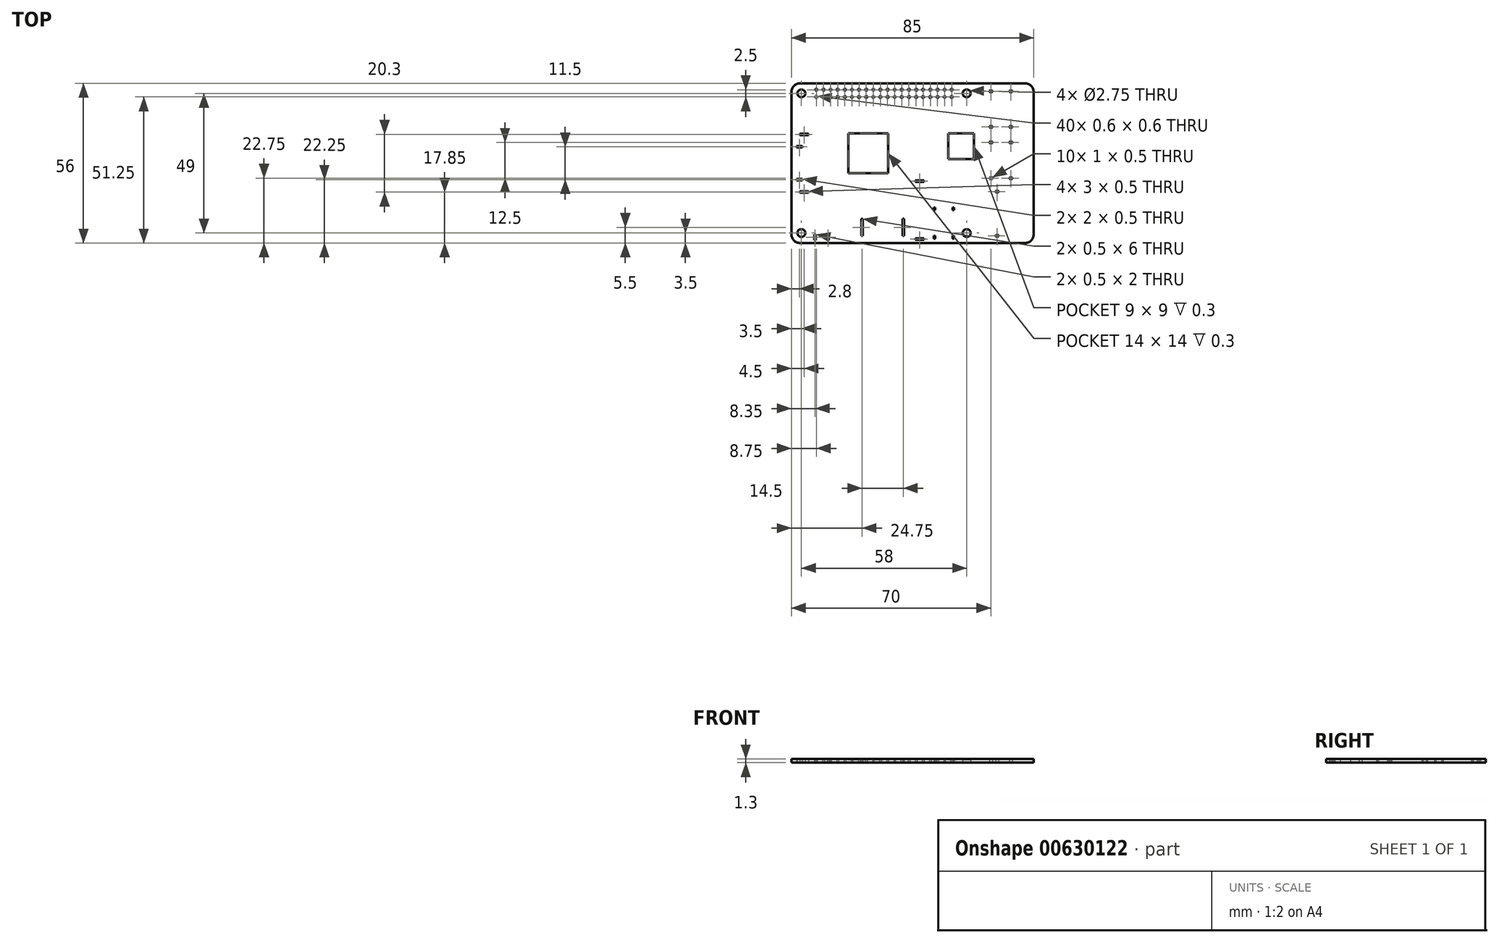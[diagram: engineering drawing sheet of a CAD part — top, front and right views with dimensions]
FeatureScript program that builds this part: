
annotation { "Feature Type Name" : "Feature", "Feature Type Description" : "" }
export const myFeature = defineFeature(function(context is Context, id is Id, definition is map)
    precondition{}
    {
        {
            var Q0;
            Q0=qCreatedBy(makeId("Top.planeOp"),FACE);
            var sketch = newSketch(context, id + "F0", { "sketchPlane" : qUnion([Q0])});
            skLineSegment(sketch, "E0.bottom", {"start": v(0, 0) * mm, "end": v(85, 0) * mm});
            skLineSegment(sketch, "E0.top", {"start": v(0, 56) * mm, "end": v(85, 56) * mm});
            skLineSegment(sketch, "E0.left", {"start": v(0, 0) * mm, "end": v(0, 56) * mm});
            skLineSegment(sketch, "E0.right", {"start": v(85, 0) * mm, "end": v(85, 56) * mm});
            skCircle(sketch, "E1", {"center": v(3.5, 52.5) * mm, "radius": 1.38 * mm});
            skCircle(sketch, "E2", {"center": v(61.5, 52.5) * mm, "radius": 1.38 * mm});
            skCircle(sketch, "E3", {"center": v(61.5, 3.5) * mm, "radius": 1.38 * mm});
            skCircle(sketch, "E4", {"center": v(3.5, 3.5) * mm, "radius": 1.37 * mm});
            skLineSegment(sketch, "E5.bottom", {"start": v(7.5, 55) * mm, "end": v(57.5, 55) * mm, "construction": true});
            skLineSegment(sketch, "E5.top", {"start": v(7.5, 50) * mm, "end": v(57.5, 50) * mm, "construction": true});
            skLineSegment(sketch, "E5.left", {"start": v(7.5, 55) * mm, "end": v(7.5, 50) * mm, "construction": true});
            skLineSegment(sketch, "E5.right", {"start": v(57.5, 55) * mm, "end": v(57.5, 50) * mm, "construction": true});
            skLineSegment(sketch, "E6", {"start": v(32.5, 55) * mm, "end": v(32.5, 50) * mm, "construction": true});
            skLineSegment(sketch, "E7", {"start": v(7.5, 52.5) * mm, "end": v(57.5, 52.5) * mm, "construction": true});
            skLineSegment(sketch, "E8.bottom", {"start": v(8.45, 54.05) * mm, "end": v(9.05, 54.05) * mm});
            skLineSegment(sketch, "E8.top", {"start": v(8.45, 53.45) * mm, "end": v(9.05, 53.45) * mm});
            skLineSegment(sketch, "E8.left", {"start": v(8.45, 54.05) * mm, "end": v(8.45, 53.45) * mm});
            skLineSegment(sketch, "E8.right", {"start": v(9.05, 54.05) * mm, "end": v(9.05, 53.45) * mm});
            skLineSegment(sketch, "E9", {"start": v(10, 55) * mm, "end": v(10, 50) * mm, "construction": true});
            skLineSegment(sketch, "E10.1.0.0", {"start": v(10.95, 53.45) * mm, "end": v(11.55, 53.45) * mm});
            skLineSegment(sketch, "E10.1.0.1", {"start": v(10.95, 54.05) * mm, "end": v(11.55, 54.05) * mm});
            skLineSegment(sketch, "E10.1.0.2", {"start": v(11.55, 54.05) * mm, "end": v(11.55, 53.45) * mm});
            skLineSegment(sketch, "E10.1.0.3", {"start": v(10.95, 54.05) * mm, "end": v(10.95, 53.45) * mm});
            skLineSegment(sketch, "E10.2.0.0", {"start": v(13.45, 53.45) * mm, "end": v(14.05, 53.45) * mm});
            skLineSegment(sketch, "E10.2.0.1", {"start": v(13.45, 54.05) * mm, "end": v(14.05, 54.05) * mm});
            skLineSegment(sketch, "E10.2.0.2", {"start": v(14.05, 54.05) * mm, "end": v(14.05, 53.45) * mm});
            skLineSegment(sketch, "E10.2.0.3", {"start": v(13.45, 54.05) * mm, "end": v(13.45, 53.45) * mm});
            skLineSegment(sketch, "E10.3.0.0", {"start": v(15.95, 53.45) * mm, "end": v(16.55, 53.45) * mm});
            skLineSegment(sketch, "E10.3.0.1", {"start": v(15.95, 54.05) * mm, "end": v(16.55, 54.05) * mm});
            skLineSegment(sketch, "E10.3.0.2", {"start": v(16.55, 54.05) * mm, "end": v(16.55, 53.45) * mm});
            skLineSegment(sketch, "E10.3.0.3", {"start": v(15.95, 54.05) * mm, "end": v(15.95, 53.45) * mm});
            skLineSegment(sketch, "E10.4.0.0", {"start": v(18.45, 53.45) * mm, "end": v(19.05, 53.45) * mm});
            skLineSegment(sketch, "E10.4.0.1", {"start": v(18.45, 54.05) * mm, "end": v(19.05, 54.05) * mm});
            skLineSegment(sketch, "E10.4.0.2", {"start": v(19.05, 54.05) * mm, "end": v(19.05, 53.45) * mm});
            skLineSegment(sketch, "E10.4.0.3", {"start": v(18.45, 54.05) * mm, "end": v(18.45, 53.45) * mm});
            skLineSegment(sketch, "E10.5.0.0", {"start": v(20.95, 53.45) * mm, "end": v(21.55, 53.45) * mm});
            skLineSegment(sketch, "E10.5.0.1", {"start": v(20.95, 54.05) * mm, "end": v(21.55, 54.05) * mm});
            skLineSegment(sketch, "E10.5.0.2", {"start": v(21.55, 54.05) * mm, "end": v(21.55, 53.45) * mm});
            skLineSegment(sketch, "E10.5.0.3", {"start": v(20.95, 54.05) * mm, "end": v(20.95, 53.45) * mm});
            skLineSegment(sketch, "E10.6.0.0", {"start": v(23.45, 53.45) * mm, "end": v(24.05, 53.45) * mm});
            skLineSegment(sketch, "E10.6.0.1", {"start": v(23.45, 54.05) * mm, "end": v(24.05, 54.05) * mm});
            skLineSegment(sketch, "E10.6.0.2", {"start": v(24.05, 54.05) * mm, "end": v(24.05, 53.45) * mm});
            skLineSegment(sketch, "E10.6.0.3", {"start": v(23.45, 54.05) * mm, "end": v(23.45, 53.45) * mm});
            skLineSegment(sketch, "E10.7.0.0", {"start": v(25.95, 53.45) * mm, "end": v(26.55, 53.45) * mm});
            skLineSegment(sketch, "E10.7.0.1", {"start": v(25.95, 54.05) * mm, "end": v(26.55, 54.05) * mm});
            skLineSegment(sketch, "E10.7.0.2", {"start": v(26.55, 54.05) * mm, "end": v(26.55, 53.45) * mm});
            skLineSegment(sketch, "E10.7.0.3", {"start": v(25.95, 54.05) * mm, "end": v(25.95, 53.45) * mm});
            skLineSegment(sketch, "E10.8.0.0", {"start": v(28.45, 53.45) * mm, "end": v(29.05, 53.45) * mm});
            skLineSegment(sketch, "E10.8.0.1", {"start": v(28.45, 54.05) * mm, "end": v(29.05, 54.05) * mm});
            skLineSegment(sketch, "E10.8.0.2", {"start": v(29.05, 54.05) * mm, "end": v(29.05, 53.45) * mm});
            skLineSegment(sketch, "E10.8.0.3", {"start": v(28.45, 54.05) * mm, "end": v(28.45, 53.45) * mm});
            skLineSegment(sketch, "E10.9.0.0", {"start": v(30.95, 53.45) * mm, "end": v(31.55, 53.45) * mm});
            skLineSegment(sketch, "E10.9.0.1", {"start": v(30.95, 54.05) * mm, "end": v(31.55, 54.05) * mm});
            skLineSegment(sketch, "E10.9.0.2", {"start": v(31.55, 54.05) * mm, "end": v(31.55, 53.45) * mm});
            skLineSegment(sketch, "E10.9.0.3", {"start": v(30.95, 54.05) * mm, "end": v(30.95, 53.45) * mm});
            skLineSegment(sketch, "E10.direction1", {"start": v(8.45, 53.45) * mm, "end": v(10.95, 53.45) * mm, "construction": true});
            skLineSegment(sketch, "E11.MirrorCS", {"start": v(28.45, 51.55) * mm, "end": v(29.05, 51.55) * mm});
            skLineSegment(sketch, "E12.MirrorCS", {"start": v(28.45, 50.95) * mm, "end": v(29.05, 50.95) * mm});
            skLineSegment(sketch, "E13.MirrorCS", {"start": v(30.95, 50.95) * mm, "end": v(31.55, 50.95) * mm});
            skLineSegment(sketch, "E14.MirrorCS", {"start": v(10.95, 50.95) * mm, "end": v(11.55, 50.95) * mm});
            skLineSegment(sketch, "E15.MirrorCS", {"start": v(10.95, 51.55) * mm, "end": v(11.55, 51.55) * mm});
            skLineSegment(sketch, "E16.MirrorCS", {"start": v(30.95, 51.55) * mm, "end": v(31.55, 51.55) * mm});
            skLineSegment(sketch, "E17.MirrorCS", {"start": v(8.45, 50.95) * mm, "end": v(9.05, 50.95) * mm});
            skLineSegment(sketch, "E18.MirrorCS", {"start": v(8.45, 51.55) * mm, "end": v(9.05, 51.55) * mm});
            skLineSegment(sketch, "E19.MirrorCS", {"start": v(9.05, 50.95) * mm, "end": v(9.05, 51.55) * mm});
            skLineSegment(sketch, "E20.MirrorCS", {"start": v(18.45, 50.95) * mm, "end": v(18.45, 51.55) * mm});
            skLineSegment(sketch, "E21.MirrorCS", {"start": v(28.45, 50.95) * mm, "end": v(28.45, 51.55) * mm});
            skLineSegment(sketch, "E22.MirrorCS", {"start": v(20.95, 50.95) * mm, "end": v(20.95, 51.55) * mm});
            skLineSegment(sketch, "E23.MirrorCS", {"start": v(18.45, 51.55) * mm, "end": v(19.05, 51.55) * mm});
            skLineSegment(sketch, "E24.MirrorCS", {"start": v(30.95, 50.95) * mm, "end": v(30.95, 51.55) * mm});
            skLineSegment(sketch, "E25.MirrorCS", {"start": v(10.95, 50.95) * mm, "end": v(10.95, 51.55) * mm});
            skLineSegment(sketch, "E26.MirrorCS", {"start": v(14.05, 50.95) * mm, "end": v(14.05, 51.55) * mm});
            skLineSegment(sketch, "E27.MirrorCS", {"start": v(24.05, 50.95) * mm, "end": v(24.05, 51.55) * mm});
            skLineSegment(sketch, "E28.MirrorCS", {"start": v(19.05, 50.95) * mm, "end": v(19.05, 51.55) * mm});
            skLineSegment(sketch, "E29.MirrorCS", {"start": v(29.05, 50.95) * mm, "end": v(29.05, 51.55) * mm});
            skLineSegment(sketch, "E30.MirrorCS", {"start": v(21.55, 50.95) * mm, "end": v(21.55, 51.55) * mm});
            skLineSegment(sketch, "E31.MirrorCS", {"start": v(15.95, 50.95) * mm, "end": v(15.95, 51.55) * mm});
            skLineSegment(sketch, "E32.MirrorCS", {"start": v(31.55, 50.95) * mm, "end": v(31.55, 51.55) * mm});
            skLineSegment(sketch, "E33.MirrorCS", {"start": v(25.95, 50.95) * mm, "end": v(25.95, 51.55) * mm});
            skLineSegment(sketch, "E34.MirrorCS", {"start": v(11.55, 50.95) * mm, "end": v(11.55, 51.55) * mm});
            skLineSegment(sketch, "E35.MirrorCS", {"start": v(13.45, 50.95) * mm, "end": v(14.05, 50.95) * mm});
            skLineSegment(sketch, "E36.MirrorCS", {"start": v(23.45, 50.95) * mm, "end": v(24.05, 50.95) * mm});
            skLineSegment(sketch, "E37.MirrorCS", {"start": v(15.95, 50.95) * mm, "end": v(16.55, 50.95) * mm});
            skLineSegment(sketch, "E38.MirrorCS", {"start": v(25.95, 50.95) * mm, "end": v(26.55, 50.95) * mm});
            skLineSegment(sketch, "E39.MirrorCS", {"start": v(18.45, 50.95) * mm, "end": v(19.05, 50.95) * mm});
            skLineSegment(sketch, "E40.MirrorCS", {"start": v(8.45, 50.95) * mm, "end": v(8.45, 51.55) * mm});
            skLineSegment(sketch, "E41.MirrorCS", {"start": v(20.95, 50.95) * mm, "end": v(21.55, 50.95) * mm});
            skLineSegment(sketch, "E42.MirrorCS", {"start": v(16.55, 50.95) * mm, "end": v(16.55, 51.55) * mm});
            skLineSegment(sketch, "E43.MirrorCS", {"start": v(26.55, 50.95) * mm, "end": v(26.55, 51.55) * mm});
            skLineSegment(sketch, "E44.MirrorCS", {"start": v(13.45, 51.55) * mm, "end": v(14.05, 51.55) * mm});
            skLineSegment(sketch, "E45.MirrorCS", {"start": v(23.45, 51.55) * mm, "end": v(24.05, 51.55) * mm});
            skLineSegment(sketch, "E46.MirrorCS", {"start": v(8.45, 51.55) * mm, "end": v(10.95, 51.55) * mm, "construction": true});
            skLineSegment(sketch, "E47.MirrorCS", {"start": v(15.95, 51.55) * mm, "end": v(16.55, 51.55) * mm});
            skLineSegment(sketch, "E48.MirrorCS", {"start": v(25.95, 51.55) * mm, "end": v(26.55, 51.55) * mm});
            skLineSegment(sketch, "E49.MirrorCS", {"start": v(13.45, 50.95) * mm, "end": v(13.45, 51.55) * mm});
            skLineSegment(sketch, "E50.MirrorCS", {"start": v(23.45, 50.95) * mm, "end": v(23.45, 51.55) * mm});
            skLineSegment(sketch, "E51.MirrorCS", {"start": v(20.95, 51.55) * mm, "end": v(21.55, 51.55) * mm});
            skLineSegment(sketch, "E52.MirrorCS", {"start": v(49.05, 50.95) * mm, "end": v(48.45, 50.95) * mm});
            skLineSegment(sketch, "E53.MirrorCS", {"start": v(41.55, 50.95) * mm, "end": v(40.95, 50.95) * mm});
            skLineSegment(sketch, "E54.MirrorCS", {"start": v(41.55, 54.05) * mm, "end": v(40.95, 54.05) * mm});
            skLineSegment(sketch, "E55.MirrorCS", {"start": v(46.55, 54.05) * mm, "end": v(45.95, 54.05) * mm});
            skLineSegment(sketch, "E56.MirrorCS", {"start": v(41.55, 53.45) * mm, "end": v(40.95, 53.45) * mm});
            skLineSegment(sketch, "E57.MirrorCS", {"start": v(44.05, 51.55) * mm, "end": v(43.45, 51.55) * mm});
            skLineSegment(sketch, "E58.MirrorCS", {"start": v(41.55, 51.55) * mm, "end": v(40.95, 51.55) * mm});
            skLineSegment(sketch, "E59.MirrorCS", {"start": v(49.05, 54.05) * mm, "end": v(48.45, 54.05) * mm});
            skLineSegment(sketch, "E60.MirrorCS", {"start": v(49.05, 51.55) * mm, "end": v(48.45, 51.55) * mm});
            skLineSegment(sketch, "E61.MirrorCS", {"start": v(44.05, 53.45) * mm, "end": v(43.45, 53.45) * mm});
            skLineSegment(sketch, "E62.MirrorCS", {"start": v(49.05, 53.45) * mm, "end": v(48.45, 53.45) * mm});
            skLineSegment(sketch, "E63.MirrorCS", {"start": v(46.55, 50.95) * mm, "end": v(45.95, 50.95) * mm});
            skLineSegment(sketch, "E64.MirrorCS", {"start": v(46.55, 51.55) * mm, "end": v(45.95, 51.55) * mm});
            skLineSegment(sketch, "E65.MirrorCS", {"start": v(44.05, 54.05) * mm, "end": v(43.45, 54.05) * mm});
            skLineSegment(sketch, "E66.MirrorCS", {"start": v(44.05, 50.95) * mm, "end": v(43.45, 50.95) * mm});
            skLineSegment(sketch, "E67.MirrorCS", {"start": v(46.55, 53.45) * mm, "end": v(45.95, 53.45) * mm});
            skLineSegment(sketch, "E68.MirrorCS", {"start": v(55.95, 54.05) * mm, "end": v(55.95, 53.45) * mm});
            skLineSegment(sketch, "E69.MirrorCS", {"start": v(56.55, 53.45) * mm, "end": v(55.95, 53.45) * mm});
            skLineSegment(sketch, "E70.MirrorCS", {"start": v(56.55, 51.55) * mm, "end": v(55.95, 51.55) * mm});
            skLineSegment(sketch, "E71.MirrorCS", {"start": v(46.55, 54.05) * mm, "end": v(46.55, 53.45) * mm});
            skLineSegment(sketch, "E72.MirrorCS", {"start": v(36.55, 54.05) * mm, "end": v(36.55, 53.45) * mm});
            skLineSegment(sketch, "E73.MirrorCS", {"start": v(36.55, 50.95) * mm, "end": v(36.55, 51.55) * mm});
            skLineSegment(sketch, "E74.MirrorCS", {"start": v(45.95, 50.95) * mm, "end": v(45.95, 51.55) * mm});
            skLineSegment(sketch, "E75.MirrorCS", {"start": v(51.55, 51.55) * mm, "end": v(50.95, 51.55) * mm});
            skLineSegment(sketch, "E76.MirrorCS", {"start": v(50.95, 54.05) * mm, "end": v(50.95, 53.45) * mm});
            skLineSegment(sketch, "E77.MirrorCS", {"start": v(40.95, 54.05) * mm, "end": v(40.95, 53.45) * mm});
            skLineSegment(sketch, "E78.MirrorCS", {"start": v(36.55, 50.95) * mm, "end": v(35.95, 50.95) * mm});
            skLineSegment(sketch, "E79.MirrorCS", {"start": v(45.95, 54.05) * mm, "end": v(45.95, 53.45) * mm});
            skLineSegment(sketch, "E80.MirrorCS", {"start": v(35.95, 54.05) * mm, "end": v(35.95, 53.45) * mm});
            skLineSegment(sketch, "E81.MirrorCS", {"start": v(46.55, 50.95) * mm, "end": v(46.55, 51.55) * mm});
            skLineSegment(sketch, "E82.MirrorCS", {"start": v(40.95, 50.95) * mm, "end": v(40.95, 51.55) * mm});
            skLineSegment(sketch, "E83.MirrorCS", {"start": v(38.45, 50.95) * mm, "end": v(38.45, 51.55) * mm});
            skLineSegment(sketch, "E84.MirrorCS", {"start": v(51.55, 54.05) * mm, "end": v(50.95, 54.05) * mm});
            skLineSegment(sketch, "E85.MirrorCS", {"start": v(36.55, 51.55) * mm, "end": v(35.95, 51.55) * mm});
            skLineSegment(sketch, "E86.MirrorCS", {"start": v(36.55, 54.05) * mm, "end": v(35.95, 54.05) * mm});
            skLineSegment(sketch, "E87.MirrorCS", {"start": v(55.95, 50.95) * mm, "end": v(55.95, 51.55) * mm});
            skLineSegment(sketch, "E88.MirrorCS", {"start": v(51.55, 50.95) * mm, "end": v(50.95, 50.95) * mm});
            skLineSegment(sketch, "E89.MirrorCS", {"start": v(56.55, 54.05) * mm, "end": v(56.55, 53.45) * mm});
            skLineSegment(sketch, "E90.MirrorCS", {"start": v(50.95, 50.95) * mm, "end": v(50.95, 51.55) * mm});
            skLineSegment(sketch, "E91.MirrorCS", {"start": v(48.45, 50.95) * mm, "end": v(48.45, 51.55) * mm});
            skLineSegment(sketch, "E92.MirrorCS", {"start": v(51.55, 53.45) * mm, "end": v(50.95, 53.45) * mm});
            skLineSegment(sketch, "E93.MirrorCS", {"start": v(56.55, 53.45) * mm, "end": v(54.05, 53.45) * mm, "construction": true});
            skLineSegment(sketch, "E94.MirrorCS", {"start": v(34.05, 50.95) * mm, "end": v(33.45, 50.95) * mm});
            skLineSegment(sketch, "E95.MirrorCS", {"start": v(41.55, 54.05) * mm, "end": v(41.55, 53.45) * mm});
            skLineSegment(sketch, "E96.MirrorCS", {"start": v(51.55, 54.05) * mm, "end": v(51.55, 53.45) * mm});
            skLineSegment(sketch, "E97.MirrorCS", {"start": v(35.95, 50.95) * mm, "end": v(35.95, 51.55) * mm});
            skLineSegment(sketch, "E98.MirrorCS", {"start": v(39.05, 54.05) * mm, "end": v(38.45, 54.05) * mm});
            skLineSegment(sketch, "E99.MirrorCS", {"start": v(54.05, 51.55) * mm, "end": v(53.45, 51.55) * mm});
            skLineSegment(sketch, "E100.MirrorCS", {"start": v(49.05, 50.95) * mm, "end": v(49.05, 51.55) * mm});
            skLineSegment(sketch, "E101.MirrorCS", {"start": v(53.45, 54.05) * mm, "end": v(53.45, 53.45) * mm});
            skLineSegment(sketch, "E102.MirrorCS", {"start": v(54.05, 53.45) * mm, "end": v(53.45, 53.45) * mm});
            skLineSegment(sketch, "E103.MirrorCS", {"start": v(39.05, 50.95) * mm, "end": v(38.45, 50.95) * mm});
            skLineSegment(sketch, "E104.MirrorCS", {"start": v(44.05, 50.95) * mm, "end": v(44.05, 51.55) * mm});
            skLineSegment(sketch, "E105.MirrorCS", {"start": v(34.05, 53.45) * mm, "end": v(33.45, 53.45) * mm});
            skLineSegment(sketch, "E106.MirrorCS", {"start": v(39.05, 50.95) * mm, "end": v(39.05, 51.55) * mm});
            skLineSegment(sketch, "E107.MirrorCS", {"start": v(56.55, 50.95) * mm, "end": v(56.55, 51.55) * mm});
            skLineSegment(sketch, "E108.MirrorCS", {"start": v(33.45, 54.05) * mm, "end": v(33.45, 53.45) * mm});
            skLineSegment(sketch, "E109.MirrorCS", {"start": v(56.55, 50.95) * mm, "end": v(55.95, 50.95) * mm});
            skLineSegment(sketch, "E110.MirrorCS", {"start": v(34.05, 50.95) * mm, "end": v(34.05, 51.55) * mm});
            skLineSegment(sketch, "E111.MirrorCS", {"start": v(39.05, 54.05) * mm, "end": v(39.05, 53.45) * mm});
            skLineSegment(sketch, "E112.MirrorCS", {"start": v(49.05, 54.05) * mm, "end": v(49.05, 53.45) * mm});
            skLineSegment(sketch, "E113.MirrorCS", {"start": v(43.45, 54.05) * mm, "end": v(43.45, 53.45) * mm});
            skLineSegment(sketch, "E114.MirrorCS", {"start": v(51.55, 50.95) * mm, "end": v(51.55, 51.55) * mm});
            skLineSegment(sketch, "E115.MirrorCS", {"start": v(54.05, 50.95) * mm, "end": v(53.45, 50.95) * mm});
            skLineSegment(sketch, "E116.MirrorCS", {"start": v(39.05, 53.45) * mm, "end": v(38.45, 53.45) * mm});
            skLineSegment(sketch, "E117.MirrorCS", {"start": v(56.55, 51.55) * mm, "end": v(54.05, 51.55) * mm, "construction": true});
            skLineSegment(sketch, "E118.MirrorCS", {"start": v(43.45, 50.95) * mm, "end": v(43.45, 51.55) * mm});
            skLineSegment(sketch, "E119.MirrorCS", {"start": v(54.05, 54.05) * mm, "end": v(53.45, 54.05) * mm});
            skLineSegment(sketch, "E120.MirrorCS", {"start": v(33.45, 50.95) * mm, "end": v(33.45, 51.55) * mm});
            skLineSegment(sketch, "E121.MirrorCS", {"start": v(34.05, 51.55) * mm, "end": v(33.45, 51.55) * mm});
            skLineSegment(sketch, "E122.MirrorCS", {"start": v(38.45, 54.05) * mm, "end": v(38.45, 53.45) * mm});
            skLineSegment(sketch, "E123.MirrorCS", {"start": v(34.05, 54.05) * mm, "end": v(33.45, 54.05) * mm});
            skLineSegment(sketch, "E124.MirrorCS", {"start": v(39.05, 51.55) * mm, "end": v(38.45, 51.55) * mm});
            skLineSegment(sketch, "E125.MirrorCS", {"start": v(56.55, 54.05) * mm, "end": v(55.95, 54.05) * mm});
            skLineSegment(sketch, "E126.MirrorCS", {"start": v(54.05, 54.05) * mm, "end": v(54.05, 53.45) * mm});
            skLineSegment(sketch, "E127.MirrorCS", {"start": v(53.45, 50.95) * mm, "end": v(53.45, 51.55) * mm});
            skLineSegment(sketch, "E128.MirrorCS", {"start": v(48.45, 54.05) * mm, "end": v(48.45, 53.45) * mm});
            skLineSegment(sketch, "E129.MirrorCS", {"start": v(54.05, 50.95) * mm, "end": v(54.05, 51.55) * mm});
            skLineSegment(sketch, "E130.MirrorCS", {"start": v(34.05, 54.05) * mm, "end": v(34.05, 53.45) * mm});
            skLineSegment(sketch, "E131.MirrorCS", {"start": v(36.55, 53.45) * mm, "end": v(35.95, 53.45) * mm});
            skLineSegment(sketch, "E132.MirrorCS", {"start": v(41.55, 50.95) * mm, "end": v(41.55, 51.55) * mm});
            skLineSegment(sketch, "E133.MirrorCS", {"start": v(44.05, 54.05) * mm, "end": v(44.05, 53.45) * mm});
            skLineSegment(sketch, "E134", {"start": v(0, 28) * mm, "end": v(85, 28) * mm, "construction": true});
            skLineSegment(sketch, "E135.bottom", {"start": v(1.8, 34) * mm, "end": v(3.8, 34) * mm});
            skLineSegment(sketch, "E135.top", {"start": v(1.8, 33.5) * mm, "end": v(3.8, 33.5) * mm});
            skLineSegment(sketch, "E135.left", {"start": v(1.8, 34) * mm, "end": v(1.8, 33.5) * mm});
            skLineSegment(sketch, "E135.right", {"start": v(3.8, 34) * mm, "end": v(3.8, 33.5) * mm});
            skLineSegment(sketch, "E136.MirrorCS", {"start": v(1.8, 22) * mm, "end": v(3.8, 22) * mm});
            skLineSegment(sketch, "E137.MirrorCS", {"start": v(3.8, 22) * mm, "end": v(3.8, 22.5) * mm});
            skLineSegment(sketch, "E138.MirrorCS", {"start": v(1.8, 22.5) * mm, "end": v(3.8, 22.5) * mm});
            skLineSegment(sketch, "E139.MirrorCS", {"start": v(1.8, 22) * mm, "end": v(1.8, 22.5) * mm});
            skLineSegment(sketch, "E140.bottom", {"start": v(24.5, 8.5) * mm, "end": v(25, 8.5) * mm});
            skLineSegment(sketch, "E140.top", {"start": v(24.5, 2.5) * mm, "end": v(25, 2.5) * mm});
            skLineSegment(sketch, "E140.left", {"start": v(24.5, 8.5) * mm, "end": v(24.5, 2.5) * mm});
            skLineSegment(sketch, "E140.right", {"start": v(25, 8.5) * mm, "end": v(25, 2.5) * mm});
            skLineSegment(sketch, "E141", {"start": v(32, 0) * mm, "end": v(32, 56) * mm, "construction": true});
            skLineSegment(sketch, "E142.MirrorCS", {"start": v(39.5, 2.5) * mm, "end": v(39, 2.5) * mm});
            skLineSegment(sketch, "E143.MirrorCS", {"start": v(39.5, 8.5) * mm, "end": v(39, 8.5) * mm});
            skLineSegment(sketch, "E144.MirrorCS", {"start": v(39.5, 8.5) * mm, "end": v(39.5, 2.5) * mm});
            skLineSegment(sketch, "E145.MirrorCS", {"start": v(39, 8.5) * mm, "end": v(39, 2.5) * mm});
            skLineSegment(sketch, "E146.bottom", {"start": v(8.1, 3) * mm, "end": v(8.6, 3) * mm});
            skLineSegment(sketch, "E146.top", {"start": v(8.1, 1) * mm, "end": v(8.6, 1) * mm});
            skLineSegment(sketch, "E146.left", {"start": v(8.1, 3) * mm, "end": v(8.1, 1) * mm});
            skLineSegment(sketch, "E146.right", {"start": v(8.6, 3) * mm, "end": v(8.6, 1) * mm});
            skLineSegment(sketch, "E147", {"start": v(10.6, 56) * mm, "end": v(10.6, 0) * mm, "construction": true});
            skLineSegment(sketch, "E148.MirrorCS", {"start": v(13.1, 1) * mm, "end": v(12.6, 1) * mm});
            skLineSegment(sketch, "E149.MirrorCS", {"start": v(13.1, 3) * mm, "end": v(12.6, 3) * mm});
            skLineSegment(sketch, "E150.MirrorCS", {"start": v(13.1, 3) * mm, "end": v(13.1, 1) * mm});
            skLineSegment(sketch, "E151.MirrorCS", {"start": v(12.6, 3) * mm, "end": v(12.6, 1) * mm});
            skLineSegment(sketch, "E152", {"start": v(53.5, 0) * mm, "end": v(53.5, 56) * mm, "construction": true});
            skLineSegment(sketch, "E153.bottom", {"start": v(50, 12.5) * mm, "end": v(50.5, 12.5) * mm});
            skLineSegment(sketch, "E153.top", {"start": v(50, 11.5) * mm, "end": v(50.5, 11.5) * mm});
            skLineSegment(sketch, "E153.left", {"start": v(50, 12.5) * mm, "end": v(50, 11.5) * mm});
            skLineSegment(sketch, "E153.right", {"start": v(50.5, 12.5) * mm, "end": v(50.5, 11.5) * mm});
            skLineSegment(sketch, "E154.bottom", {"start": v(50, 2.5) * mm, "end": v(50.5, 2.5) * mm});
            skLineSegment(sketch, "E154.top", {"start": v(50, 1.5) * mm, "end": v(50.5, 1.5) * mm});
            skLineSegment(sketch, "E154.left", {"start": v(50, 2.5) * mm, "end": v(50, 1.5) * mm});
            skLineSegment(sketch, "E154.right", {"start": v(50.5, 2.5) * mm, "end": v(50.5, 1.5) * mm});
            skLineSegment(sketch, "E155.MirrorCS", {"start": v(57, 11.5) * mm, "end": v(56.5, 11.5) * mm});
            skLineSegment(sketch, "E156.MirrorCS", {"start": v(57, 12.5) * mm, "end": v(56.5, 12.5) * mm});
            skLineSegment(sketch, "E157.MirrorCS", {"start": v(57, 1.5) * mm, "end": v(56.5, 1.5) * mm});
            skLineSegment(sketch, "E158.MirrorCS", {"start": v(57, 2.5) * mm, "end": v(56.5, 2.5) * mm});
            skLineSegment(sketch, "E159.MirrorCS", {"start": v(56.5, 2.5) * mm, "end": v(56.5, 1.5) * mm});
            skLineSegment(sketch, "E160.MirrorCS", {"start": v(57, 2.5) * mm, "end": v(57, 1.5) * mm});
            skLineSegment(sketch, "E161.MirrorCS", {"start": v(57, 12.5) * mm, "end": v(57, 11.5) * mm});
            skLineSegment(sketch, "E162.MirrorCS", {"start": v(56.5, 12.5) * mm, "end": v(56.5, 11.5) * mm});
            skLineSegment(sketch, "E163", {"start": v(0, 47) * mm, "end": v(85, 47) * mm, "construction": true});
            skLineSegment(sketch, "E164.bottom", {"start": v(69.5, 53.5) * mm, "end": v(70.5, 53.5) * mm});
            skLineSegment(sketch, "E164.top", {"start": v(69.5, 53) * mm, "end": v(70.5, 53) * mm});
            skLineSegment(sketch, "E164.left", {"start": v(69.5, 53.5) * mm, "end": v(69.5, 53) * mm});
            skLineSegment(sketch, "E164.right", {"start": v(70.5, 53.5) * mm, "end": v(70.5, 53) * mm});
            skLineSegment(sketch, "E165.bottom", {"start": v(76.5, 53.5) * mm, "end": v(77.5, 53.5) * mm});
            skLineSegment(sketch, "E165.top", {"start": v(76.5, 53) * mm, "end": v(77.5, 53) * mm});
            skLineSegment(sketch, "E165.left", {"start": v(76.5, 53.5) * mm, "end": v(76.5, 53) * mm});
            skLineSegment(sketch, "E165.right", {"start": v(77.5, 53.5) * mm, "end": v(77.5, 53) * mm});
            skLineSegment(sketch, "E166.MirrorCS", {"start": v(69.5, 40.5) * mm, "end": v(69.5, 41) * mm});
            skLineSegment(sketch, "E167.MirrorCS", {"start": v(76.5, 40.5) * mm, "end": v(76.5, 41) * mm});
            skLineSegment(sketch, "E168.MirrorCS", {"start": v(77.5, 40.5) * mm, "end": v(77.5, 41) * mm});
            skLineSegment(sketch, "E169.MirrorCS", {"start": v(70.5, 40.5) * mm, "end": v(70.5, 41) * mm});
            skLineSegment(sketch, "E170.MirrorCS", {"start": v(69.5, 40.5) * mm, "end": v(70.5, 40.5) * mm});
            skLineSegment(sketch, "E171.MirrorCS", {"start": v(69.5, 41) * mm, "end": v(70.5, 41) * mm});
            skLineSegment(sketch, "E172.MirrorCS", {"start": v(76.5, 40.5) * mm, "end": v(77.5, 40.5) * mm});
            skLineSegment(sketch, "E173.MirrorCS", {"start": v(76.5, 41) * mm, "end": v(77.5, 41) * mm});
            skLineSegment(sketch, "E174", {"start": v(0, 29) * mm, "end": v(85, 29) * mm, "construction": true});
            skLineSegment(sketch, "E175.bottom", {"start": v(69.5, 35) * mm, "end": v(70.5, 35) * mm});
            skLineSegment(sketch, "E175.top", {"start": v(69.5, 35.5) * mm, "end": v(70.5, 35.5) * mm});
            skLineSegment(sketch, "E175.left", {"start": v(69.5, 35) * mm, "end": v(69.5, 35.5) * mm});
            skLineSegment(sketch, "E175.right", {"start": v(70.5, 35) * mm, "end": v(70.5, 35.5) * mm});
            skLineSegment(sketch, "E176.bottom", {"start": v(76.5, 35) * mm, "end": v(77.5, 35) * mm});
            skLineSegment(sketch, "E176.top", {"start": v(76.5, 35.5) * mm, "end": v(77.5, 35.5) * mm});
            skLineSegment(sketch, "E176.left", {"start": v(76.5, 35) * mm, "end": v(76.5, 35.5) * mm});
            skLineSegment(sketch, "E176.right", {"start": v(77.5, 35) * mm, "end": v(77.5, 35.5) * mm});
            skLineSegment(sketch, "E177.MirrorCS", {"start": v(77.5, 23) * mm, "end": v(77.5, 22.5) * mm});
            skLineSegment(sketch, "E178.MirrorCS", {"start": v(76.5, 23) * mm, "end": v(76.5, 22.5) * mm});
            skLineSegment(sketch, "E179.MirrorCS", {"start": v(69.5, 23) * mm, "end": v(69.5, 22.5) * mm});
            skLineSegment(sketch, "E180.MirrorCS", {"start": v(70.5, 23) * mm, "end": v(70.5, 22.5) * mm});
            skLineSegment(sketch, "E181.MirrorCS", {"start": v(76.5, 22.5) * mm, "end": v(77.5, 22.5) * mm});
            skLineSegment(sketch, "E182.MirrorCS", {"start": v(69.5, 23) * mm, "end": v(70.5, 23) * mm});
            skLineSegment(sketch, "E183.MirrorCS", {"start": v(69.5, 22.5) * mm, "end": v(70.5, 22.5) * mm});
            skLineSegment(sketch, "E184.MirrorCS", {"start": v(76.5, 23) * mm, "end": v(77.5, 23) * mm});
            skLineSegment(sketch, "E185", {"start": v(0, 10.25) * mm, "end": v(85, 10.25) * mm, "construction": true});
            skLineSegment(sketch, "E186.bottom", {"start": v(71.7, 17.75) * mm, "end": v(72.7, 17.75) * mm});
            skLineSegment(sketch, "E186.top", {"start": v(71.7, 18.25) * mm, "end": v(72.7, 18.25) * mm});
            skLineSegment(sketch, "E186.left", {"start": v(71.7, 17.75) * mm, "end": v(71.7, 18.25) * mm});
            skLineSegment(sketch, "E186.right", {"start": v(72.7, 17.75) * mm, "end": v(72.7, 18.25) * mm});
            skLineSegment(sketch, "E187.MirrorCS", {"start": v(71.7, 2.75) * mm, "end": v(71.7, 2.25) * mm});
            skLineSegment(sketch, "E188.MirrorCS", {"start": v(72.7, 2.75) * mm, "end": v(72.7, 2.25) * mm});
            skLineSegment(sketch, "E189.MirrorCS", {"start": v(71.7, 2.75) * mm, "end": v(72.7, 2.75) * mm});
            skLineSegment(sketch, "E190.MirrorCS", {"start": v(71.7, 2.25) * mm, "end": v(72.7, 2.25) * mm});
            skLineSegment(sketch, "E191.bottom", {"start": v(3, 38.4) * mm, "end": v(6, 38.4) * mm});
            skLineSegment(sketch, "E191.top", {"start": v(3, 37.9) * mm, "end": v(6, 37.9) * mm});
            skLineSegment(sketch, "E191.left", {"start": v(3, 38.4) * mm, "end": v(3, 37.9) * mm});
            skLineSegment(sketch, "E191.right", {"start": v(6, 38.4) * mm, "end": v(6, 37.9) * mm});
            skLineSegment(sketch, "E192.MirrorCS", {"start": v(6, 17.6) * mm, "end": v(6, 18.1) * mm});
            skLineSegment(sketch, "E193.MirrorCS", {"start": v(3, 17.6) * mm, "end": v(3, 18.1) * mm});
            skLineSegment(sketch, "E194.MirrorCS", {"start": v(3, 18.1) * mm, "end": v(6, 18.1) * mm});
            skLineSegment(sketch, "E195.MirrorCS", {"start": v(3, 17.6) * mm, "end": v(6, 17.6) * mm});
            skLineSegment(sketch, "E196", {"start": v(0, 11.5) * mm, "end": v(85, 11.5) * mm, "construction": true});
            skLineSegment(sketch, "E197.bottom", {"start": v(43.5, 21.4) * mm, "end": v(46.5, 21.4) * mm});
            skLineSegment(sketch, "E197.top", {"start": v(43.5, 21.9) * mm, "end": v(46.5, 21.9) * mm});
            skLineSegment(sketch, "E197.left", {"start": v(43.5, 21.4) * mm, "end": v(43.5, 21.9) * mm});
            skLineSegment(sketch, "E197.right", {"start": v(46.5, 21.4) * mm, "end": v(46.5, 21.9) * mm});
            skLineSegment(sketch, "E198.MirrorCS", {"start": v(46.5, 1.6) * mm, "end": v(46.5, 1.1) * mm});
            skLineSegment(sketch, "E199.MirrorCS", {"start": v(43.5, 1.6) * mm, "end": v(43.5, 1.1) * mm});
            skLineSegment(sketch, "E200.MirrorCS", {"start": v(43.5, 1.1) * mm, "end": v(46.5, 1.1) * mm});
            skLineSegment(sketch, "E201.MirrorCS", {"start": v(43.5, 1.6) * mm, "end": v(46.5, 1.6) * mm});
            skSolve(sketch);
        }
        {
            var Q0;
            Q0=qSketchRegion(id+"F0",true);
            extrude(context, id + "F1", {"entities" : qUnion([Q0]), "depth" : 1.3 * mm});
        }
        {
            var Q0;
            Q0=makeQuery(id+"F1.opExtrude","SWEPT_EDGE",EDGE,{"disambiguationData":[OSD([sQuery(id+"F0.wireOp",EDGE,"E0.bottom"),sQuery(id+"F0.wireOp",EDGE,"E0.left")])]});
            var Q1;
            Q1=makeQuery(id+"F1.opExtrude","SWEPT_EDGE",EDGE,{"disambiguationData":[OSD([sQuery(id+"F0.wireOp",EDGE,"E0.top"),sQuery(id+"F0.wireOp",EDGE,"E0.left")])]});
            var Q2;
            Q2=makeQuery(id+"F1.opExtrude","SWEPT_EDGE",EDGE,{"disambiguationData":[OSD([sQuery(id+"F0.wireOp",EDGE,"E0.bottom"),sQuery(id+"F0.wireOp",EDGE,"E0.right")])]});
            var Q3;
            Q3=makeQuery(id+"F1.opExtrude","SWEPT_EDGE",EDGE,{"disambiguationData":[OSD([sQuery(id+"F0.wireOp",EDGE,"E0.top"),sQuery(id+"F0.wireOp",EDGE,"E0.right")])]});
            fillet(context, id + "F2", {"entities" : qUnion([Q0, Q1, Q2, Q3]), "radius" : 3 * mm, "tangentPropagation" : true, "allowEdgeOverflow" : false});
        }
        {
            var Q0;
            Q0=makeQuery(id+"F1.opExtrude","CAP_FACE",FACE,{"disambiguationData":[OSD([sQuery(id+"F0.wireOp",EDGE,"E0.bottom"),sQuery(id+"F0.wireOp",EDGE,"E0.top"),sQuery(id+"F0.wireOp",EDGE,"E0.left"),sQuery(id+"F0.wireOp",EDGE,"E0.right"),sQuery(id+"F0.wireOp",EDGE,"E1"),sQuery(id+"F0.wireOp",EDGE,"E2"),sQuery(id+"F0.wireOp",EDGE,"E3"),sQuery(id+"F0.wireOp",EDGE,"E4"),sQuery(id+"F0.wireOp",EDGE,"E8.bottom"),sQuery(id+"F0.wireOp",EDGE,"E8.top"),sQuery(id+"F0.wireOp",EDGE,"E8.left"),sQuery(id+"F0.wireOp",EDGE,"E8.right"),sQuery(id+"F0.wireOp",EDGE,"E10.1.0.0"),sQuery(id+"F0.wireOp",EDGE,"E10.1.0.1"),sQuery(id+"F0.wireOp",EDGE,"E10.1.0.2"),sQuery(id+"F0.wireOp",EDGE,"E10.1.0.3"),sQuery(id+"F0.wireOp",EDGE,"E10.2.0.0"),sQuery(id+"F0.wireOp",EDGE,"E10.2.0.1"),sQuery(id+"F0.wireOp",EDGE,"E10.2.0.2"),sQuery(id+"F0.wireOp",EDGE,"E10.2.0.3"),sQuery(id+"F0.wireOp",EDGE,"E10.3.0.0"),sQuery(id+"F0.wireOp",EDGE,"E10.3.0.1"),sQuery(id+"F0.wireOp",EDGE,"E10.3.0.2"),sQuery(id+"F0.wireOp",EDGE,"E10.3.0.3"),sQuery(id+"F0.wireOp",EDGE,"E10.4.0.0"),sQuery(id+"F0.wireOp",EDGE,"E10.4.0.1"),sQuery(id+"F0.wireOp",EDGE,"E10.4.0.2"),sQuery(id+"F0.wireOp",EDGE,"E10.4.0.3"),sQuery(id+"F0.wireOp",EDGE,"E10.5.0.0"),sQuery(id+"F0.wireOp",EDGE,"E10.5.0.1"),sQuery(id+"F0.wireOp",EDGE,"E10.5.0.2"),sQuery(id+"F0.wireOp",EDGE,"E10.5.0.3"),sQuery(id+"F0.wireOp",EDGE,"E10.6.0.0"),sQuery(id+"F0.wireOp",EDGE,"E10.6.0.1"),sQuery(id+"F0.wireOp",EDGE,"E10.6.0.2"),sQuery(id+"F0.wireOp",EDGE,"E10.6.0.3"),sQuery(id+"F0.wireOp",EDGE,"E10.7.0.0"),sQuery(id+"F0.wireOp",EDGE,"E10.7.0.1"),sQuery(id+"F0.wireOp",EDGE,"E10.7.0.2"),sQuery(id+"F0.wireOp",EDGE,"E10.7.0.3"),sQuery(id+"F0.wireOp",EDGE,"E10.8.0.0"),sQuery(id+"F0.wireOp",EDGE,"E10.8.0.1"),sQuery(id+"F0.wireOp",EDGE,"E10.8.0.2"),sQuery(id+"F0.wireOp",EDGE,"E10.8.0.3"),sQuery(id+"F0.wireOp",EDGE,"E10.9.0.0"),sQuery(id+"F0.wireOp",EDGE,"E10.9.0.1"),sQuery(id+"F0.wireOp",EDGE,"E10.9.0.2"),sQuery(id+"F0.wireOp",EDGE,"E10.9.0.3"),sQuery(id+"F0.wireOp",EDGE,"E11.MirrorCS"),sQuery(id+"F0.wireOp",EDGE,"E12.MirrorCS"),sQuery(id+"F0.wireOp",EDGE,"E13.MirrorCS"),sQuery(id+"F0.wireOp",EDGE,"E14.MirrorCS"),sQuery(id+"F0.wireOp",EDGE,"E15.MirrorCS"),sQuery(id+"F0.wireOp",EDGE,"E16.MirrorCS"),sQuery(id+"F0.wireOp",EDGE,"E17.MirrorCS"),sQuery(id+"F0.wireOp",EDGE,"E18.MirrorCS"),sQuery(id+"F0.wireOp",EDGE,"E19.MirrorCS"),sQuery(id+"F0.wireOp",EDGE,"E20.MirrorCS"),sQuery(id+"F0.wireOp",EDGE,"E21.MirrorCS"),sQuery(id+"F0.wireOp",EDGE,"E22.MirrorCS"),sQuery(id+"F0.wireOp",EDGE,"E23.MirrorCS"),sQuery(id+"F0.wireOp",EDGE,"E24.MirrorCS"),sQuery(id+"F0.wireOp",EDGE,"E25.MirrorCS"),sQuery(id+"F0.wireOp",EDGE,"E26.MirrorCS"),sQuery(id+"F0.wireOp",EDGE,"E27.MirrorCS"),sQuery(id+"F0.wireOp",EDGE,"E28.MirrorCS"),sQuery(id+"F0.wireOp",EDGE,"E29.MirrorCS"),sQuery(id+"F0.wireOp",EDGE,"E30.MirrorCS"),sQuery(id+"F0.wireOp",EDGE,"E31.MirrorCS"),sQuery(id+"F0.wireOp",EDGE,"E32.MirrorCS"),sQuery(id+"F0.wireOp",EDGE,"E33.MirrorCS"),sQuery(id+"F0.wireOp",EDGE,"E34.MirrorCS"),sQuery(id+"F0.wireOp",EDGE,"E35.MirrorCS"),sQuery(id+"F0.wireOp",EDGE,"E36.MirrorCS"),sQuery(id+"F0.wireOp",EDGE,"E37.MirrorCS"),sQuery(id+"F0.wireOp",EDGE,"E38.MirrorCS"),sQuery(id+"F0.wireOp",EDGE,"E39.MirrorCS"),sQuery(id+"F0.wireOp",EDGE,"E40.MirrorCS"),sQuery(id+"F0.wireOp",EDGE,"E41.MirrorCS"),sQuery(id+"F0.wireOp",EDGE,"E42.MirrorCS"),sQuery(id+"F0.wireOp",EDGE,"E43.MirrorCS"),sQuery(id+"F0.wireOp",EDGE,"E44.MirrorCS"),sQuery(id+"F0.wireOp",EDGE,"E45.MirrorCS"),sQuery(id+"F0.wireOp",EDGE,"E47.MirrorCS"),sQuery(id+"F0.wireOp",EDGE,"E48.MirrorCS"),sQuery(id+"F0.wireOp",EDGE,"E49.MirrorCS"),sQuery(id+"F0.wireOp",EDGE,"E50.MirrorCS"),sQuery(id+"F0.wireOp",EDGE,"E51.MirrorCS"),sQuery(id+"F0.wireOp",EDGE,"E52.MirrorCS"),sQuery(id+"F0.wireOp",EDGE,"E53.MirrorCS"),sQuery(id+"F0.wireOp",EDGE,"E54.MirrorCS"),sQuery(id+"F0.wireOp",EDGE,"E55.MirrorCS"),sQuery(id+"F0.wireOp",EDGE,"E56.MirrorCS"),sQuery(id+"F0.wireOp",EDGE,"E57.MirrorCS"),sQuery(id+"F0.wireOp",EDGE,"E58.MirrorCS"),sQuery(id+"F0.wireOp",EDGE,"E59.MirrorCS"),sQuery(id+"F0.wireOp",EDGE,"E60.MirrorCS"),sQuery(id+"F0.wireOp",EDGE,"E61.MirrorCS"),sQuery(id+"F0.wireOp",EDGE,"E62.MirrorCS"),sQuery(id+"F0.wireOp",EDGE,"E63.MirrorCS"),sQuery(id+"F0.wireOp",EDGE,"E64.MirrorCS"),sQuery(id+"F0.wireOp",EDGE,"E65.MirrorCS"),sQuery(id+"F0.wireOp",EDGE,"E66.MirrorCS"),sQuery(id+"F0.wireOp",EDGE,"E67.MirrorCS"),sQuery(id+"F0.wireOp",EDGE,"E68.MirrorCS"),sQuery(id+"F0.wireOp",EDGE,"E69.MirrorCS"),sQuery(id+"F0.wireOp",EDGE,"E70.MirrorCS"),sQuery(id+"F0.wireOp",EDGE,"E71.MirrorCS"),sQuery(id+"F0.wireOp",EDGE,"E72.MirrorCS"),sQuery(id+"F0.wireOp",EDGE,"E73.MirrorCS"),sQuery(id+"F0.wireOp",EDGE,"E74.MirrorCS"),sQuery(id+"F0.wireOp",EDGE,"E75.MirrorCS"),sQuery(id+"F0.wireOp",EDGE,"E76.MirrorCS"),sQuery(id+"F0.wireOp",EDGE,"E77.MirrorCS"),sQuery(id+"F0.wireOp",EDGE,"E78.MirrorCS"),sQuery(id+"F0.wireOp",EDGE,"E79.MirrorCS"),sQuery(id+"F0.wireOp",EDGE,"E80.MirrorCS"),sQuery(id+"F0.wireOp",EDGE,"E81.MirrorCS"),sQuery(id+"F0.wireOp",EDGE,"E82.MirrorCS"),sQuery(id+"F0.wireOp",EDGE,"E83.MirrorCS"),sQuery(id+"F0.wireOp",EDGE,"E84.MirrorCS"),sQuery(id+"F0.wireOp",EDGE,"E85.MirrorCS"),sQuery(id+"F0.wireOp",EDGE,"E86.MirrorCS"),sQuery(id+"F0.wireOp",EDGE,"E87.MirrorCS"),sQuery(id+"F0.wireOp",EDGE,"E88.MirrorCS"),sQuery(id+"F0.wireOp",EDGE,"E89.MirrorCS"),sQuery(id+"F0.wireOp",EDGE,"E90.MirrorCS"),sQuery(id+"F0.wireOp",EDGE,"E91.MirrorCS"),sQuery(id+"F0.wireOp",EDGE,"E92.MirrorCS"),sQuery(id+"F0.wireOp",EDGE,"E94.MirrorCS"),sQuery(id+"F0.wireOp",EDGE,"E95.MirrorCS"),sQuery(id+"F0.wireOp",EDGE,"E96.MirrorCS"),sQuery(id+"F0.wireOp",EDGE,"E97.MirrorCS"),sQuery(id+"F0.wireOp",EDGE,"E98.MirrorCS"),sQuery(id+"F0.wireOp",EDGE,"E99.MirrorCS"),sQuery(id+"F0.wireOp",EDGE,"E100.MirrorCS"),sQuery(id+"F0.wireOp",EDGE,"E101.MirrorCS"),sQuery(id+"F0.wireOp",EDGE,"E102.MirrorCS"),sQuery(id+"F0.wireOp",EDGE,"E103.MirrorCS"),sQuery(id+"F0.wireOp",EDGE,"E104.MirrorCS"),sQuery(id+"F0.wireOp",EDGE,"E105.MirrorCS"),sQuery(id+"F0.wireOp",EDGE,"E106.MirrorCS"),sQuery(id+"F0.wireOp",EDGE,"E107.MirrorCS"),sQuery(id+"F0.wireOp",EDGE,"E108.MirrorCS"),sQuery(id+"F0.wireOp",EDGE,"E109.MirrorCS"),sQuery(id+"F0.wireOp",EDGE,"E110.MirrorCS"),sQuery(id+"F0.wireOp",EDGE,"E111.MirrorCS"),sQuery(id+"F0.wireOp",EDGE,"E112.MirrorCS"),sQuery(id+"F0.wireOp",EDGE,"E113.MirrorCS"),sQuery(id+"F0.wireOp",EDGE,"E114.MirrorCS"),sQuery(id+"F0.wireOp",EDGE,"E115.MirrorCS"),sQuery(id+"F0.wireOp",EDGE,"E116.MirrorCS"),sQuery(id+"F0.wireOp",EDGE,"E118.MirrorCS"),sQuery(id+"F0.wireOp",EDGE,"E119.MirrorCS"),sQuery(id+"F0.wireOp",EDGE,"E120.MirrorCS"),sQuery(id+"F0.wireOp",EDGE,"E121.MirrorCS"),sQuery(id+"F0.wireOp",EDGE,"E122.MirrorCS"),sQuery(id+"F0.wireOp",EDGE,"E123.MirrorCS"),sQuery(id+"F0.wireOp",EDGE,"E124.MirrorCS"),sQuery(id+"F0.wireOp",EDGE,"E125.MirrorCS"),sQuery(id+"F0.wireOp",EDGE,"E126.MirrorCS"),sQuery(id+"F0.wireOp",EDGE,"E127.MirrorCS"),sQuery(id+"F0.wireOp",EDGE,"E128.MirrorCS"),sQuery(id+"F0.wireOp",EDGE,"E129.MirrorCS"),sQuery(id+"F0.wireOp",EDGE,"E130.MirrorCS"),sQuery(id+"F0.wireOp",EDGE,"E131.MirrorCS"),sQuery(id+"F0.wireOp",EDGE,"E132.MirrorCS"),sQuery(id+"F0.wireOp",EDGE,"E133.MirrorCS"),sQuery(id+"F0.wireOp",EDGE,"E135.bottom"),sQuery(id+"F0.wireOp",EDGE,"E135.top"),sQuery(id+"F0.wireOp",EDGE,"E135.left"),sQuery(id+"F0.wireOp",EDGE,"E135.right"),sQuery(id+"F0.wireOp",EDGE,"E136.MirrorCS"),sQuery(id+"F0.wireOp",EDGE,"E137.MirrorCS"),sQuery(id+"F0.wireOp",EDGE,"E138.MirrorCS"),sQuery(id+"F0.wireOp",EDGE,"E139.MirrorCS"),sQuery(id+"F0.wireOp",EDGE,"E140.bottom"),sQuery(id+"F0.wireOp",EDGE,"E140.top"),sQuery(id+"F0.wireOp",EDGE,"E140.left"),sQuery(id+"F0.wireOp",EDGE,"E140.right"),sQuery(id+"F0.wireOp",EDGE,"E142.MirrorCS"),sQuery(id+"F0.wireOp",EDGE,"E143.MirrorCS"),sQuery(id+"F0.wireOp",EDGE,"E144.MirrorCS"),sQuery(id+"F0.wireOp",EDGE,"E145.MirrorCS"),sQuery(id+"F0.wireOp",EDGE,"E146.bottom"),sQuery(id+"F0.wireOp",EDGE,"E146.top"),sQuery(id+"F0.wireOp",EDGE,"E146.left"),sQuery(id+"F0.wireOp",EDGE,"E146.right"),sQuery(id+"F0.wireOp",EDGE,"E148.MirrorCS"),sQuery(id+"F0.wireOp",EDGE,"E149.MirrorCS"),sQuery(id+"F0.wireOp",EDGE,"E150.MirrorCS"),sQuery(id+"F0.wireOp",EDGE,"E151.MirrorCS"),sQuery(id+"F0.wireOp",EDGE,"E153.bottom"),sQuery(id+"F0.wireOp",EDGE,"E153.top"),sQuery(id+"F0.wireOp",EDGE,"E153.left"),sQuery(id+"F0.wireOp",EDGE,"E153.right"),sQuery(id+"F0.wireOp",EDGE,"E154.bottom"),sQuery(id+"F0.wireOp",EDGE,"E154.top"),sQuery(id+"F0.wireOp",EDGE,"E154.left"),sQuery(id+"F0.wireOp",EDGE,"E154.right"),sQuery(id+"F0.wireOp",EDGE,"E155.MirrorCS"),sQuery(id+"F0.wireOp",EDGE,"E156.MirrorCS"),sQuery(id+"F0.wireOp",EDGE,"E157.MirrorCS"),sQuery(id+"F0.wireOp",EDGE,"E158.MirrorCS"),sQuery(id+"F0.wireOp",EDGE,"E159.MirrorCS"),sQuery(id+"F0.wireOp",EDGE,"E160.MirrorCS"),sQuery(id+"F0.wireOp",EDGE,"E161.MirrorCS"),sQuery(id+"F0.wireOp",EDGE,"E162.MirrorCS"),sQuery(id+"F0.wireOp",EDGE,"E164.bottom"),sQuery(id+"F0.wireOp",EDGE,"E164.top"),sQuery(id+"F0.wireOp",EDGE,"E164.left"),sQuery(id+"F0.wireOp",EDGE,"E164.right"),sQuery(id+"F0.wireOp",EDGE,"E165.bottom"),sQuery(id+"F0.wireOp",EDGE,"E165.top"),sQuery(id+"F0.wireOp",EDGE,"E165.left"),sQuery(id+"F0.wireOp",EDGE,"E165.right"),sQuery(id+"F0.wireOp",EDGE,"E166.MirrorCS"),sQuery(id+"F0.wireOp",EDGE,"E167.MirrorCS"),sQuery(id+"F0.wireOp",EDGE,"E168.MirrorCS"),sQuery(id+"F0.wireOp",EDGE,"E169.MirrorCS"),sQuery(id+"F0.wireOp",EDGE,"E170.MirrorCS"),sQuery(id+"F0.wireOp",EDGE,"E171.MirrorCS"),sQuery(id+"F0.wireOp",EDGE,"E172.MirrorCS"),sQuery(id+"F0.wireOp",EDGE,"E173.MirrorCS"),sQuery(id+"F0.wireOp",EDGE,"E175.bottom"),sQuery(id+"F0.wireOp",EDGE,"E175.top"),sQuery(id+"F0.wireOp",EDGE,"E175.left"),sQuery(id+"F0.wireOp",EDGE,"E175.right"),sQuery(id+"F0.wireOp",EDGE,"E176.bottom"),sQuery(id+"F0.wireOp",EDGE,"E176.top"),sQuery(id+"F0.wireOp",EDGE,"E176.left"),sQuery(id+"F0.wireOp",EDGE,"E176.right"),sQuery(id+"F0.wireOp",EDGE,"E177.MirrorCS"),sQuery(id+"F0.wireOp",EDGE,"E178.MirrorCS"),sQuery(id+"F0.wireOp",EDGE,"E179.MirrorCS"),sQuery(id+"F0.wireOp",EDGE,"E180.MirrorCS"),sQuery(id+"F0.wireOp",EDGE,"E181.MirrorCS"),sQuery(id+"F0.wireOp",EDGE,"E182.MirrorCS"),sQuery(id+"F0.wireOp",EDGE,"E183.MirrorCS"),sQuery(id+"F0.wireOp",EDGE,"E184.MirrorCS"),sQuery(id+"F0.wireOp",EDGE,"E186.bottom"),sQuery(id+"F0.wireOp",EDGE,"E186.top"),sQuery(id+"F0.wireOp",EDGE,"E186.left"),sQuery(id+"F0.wireOp",EDGE,"E186.right"),sQuery(id+"F0.wireOp",EDGE,"E187.MirrorCS"),sQuery(id+"F0.wireOp",EDGE,"E188.MirrorCS"),sQuery(id+"F0.wireOp",EDGE,"E189.MirrorCS"),sQuery(id+"F0.wireOp",EDGE,"E190.MirrorCS"),sQuery(id+"F0.wireOp",EDGE,"E191.bottom"),sQuery(id+"F0.wireOp",EDGE,"E191.top"),sQuery(id+"F0.wireOp",EDGE,"E191.left"),sQuery(id+"F0.wireOp",EDGE,"E191.right"),sQuery(id+"F0.wireOp",EDGE,"E192.MirrorCS"),sQuery(id+"F0.wireOp",EDGE,"E193.MirrorCS"),sQuery(id+"F0.wireOp",EDGE,"E194.MirrorCS"),sQuery(id+"F0.wireOp",EDGE,"E195.MirrorCS"),sQuery(id+"F0.wireOp",EDGE,"E197.bottom"),sQuery(id+"F0.wireOp",EDGE,"E197.top"),sQuery(id+"F0.wireOp",EDGE,"E197.left"),sQuery(id+"F0.wireOp",EDGE,"E197.right"),sQuery(id+"F0.wireOp",EDGE,"E198.MirrorCS"),sQuery(id+"F0.wireOp",EDGE,"E199.MirrorCS"),sQuery(id+"F0.wireOp",EDGE,"E200.MirrorCS"),sQuery(id+"F0.wireOp",EDGE,"E201.MirrorCS")])],"isStart":false});
            var sketch = newSketch(context, id + "F3", { "sketchPlane" : qUnion([Q0])});
            skLineSegment(sketch, "E202.bottom", {"start": v(20, 38.5) * mm, "end": v(34, 38.5) * mm});
            skLineSegment(sketch, "E202.top", {"start": v(20, 24.5) * mm, "end": v(34, 24.5) * mm});
            skLineSegment(sketch, "E202.left", {"start": v(20, 38.5) * mm, "end": v(20, 24.5) * mm});
            skLineSegment(sketch, "E202.right", {"start": v(34, 38.5) * mm, "end": v(34, 24.5) * mm});
            skLineSegment(sketch, "E203.bottom", {"start": v(55, 38.5) * mm, "end": v(64, 38.5) * mm});
            skLineSegment(sketch, "E203.top", {"start": v(55, 29.5) * mm, "end": v(64, 29.5) * mm});
            skLineSegment(sketch, "E203.left", {"start": v(55, 38.5) * mm, "end": v(55, 29.5) * mm});
            skLineSegment(sketch, "E203.right", {"start": v(64, 38.5) * mm, "end": v(64, 29.5) * mm});
            skSolve(sketch);
        }
        {
            var Q0;
            Q0=qSketchRegion(id+"F3",true);
            extrude(context, id + "F4", {"entities" : qUnion([Q0]), "operationType" : NewBodyOperationType.REMOVE, "oppositeDirection" : true, "depth" : 0.3 * mm});
        }
    });
